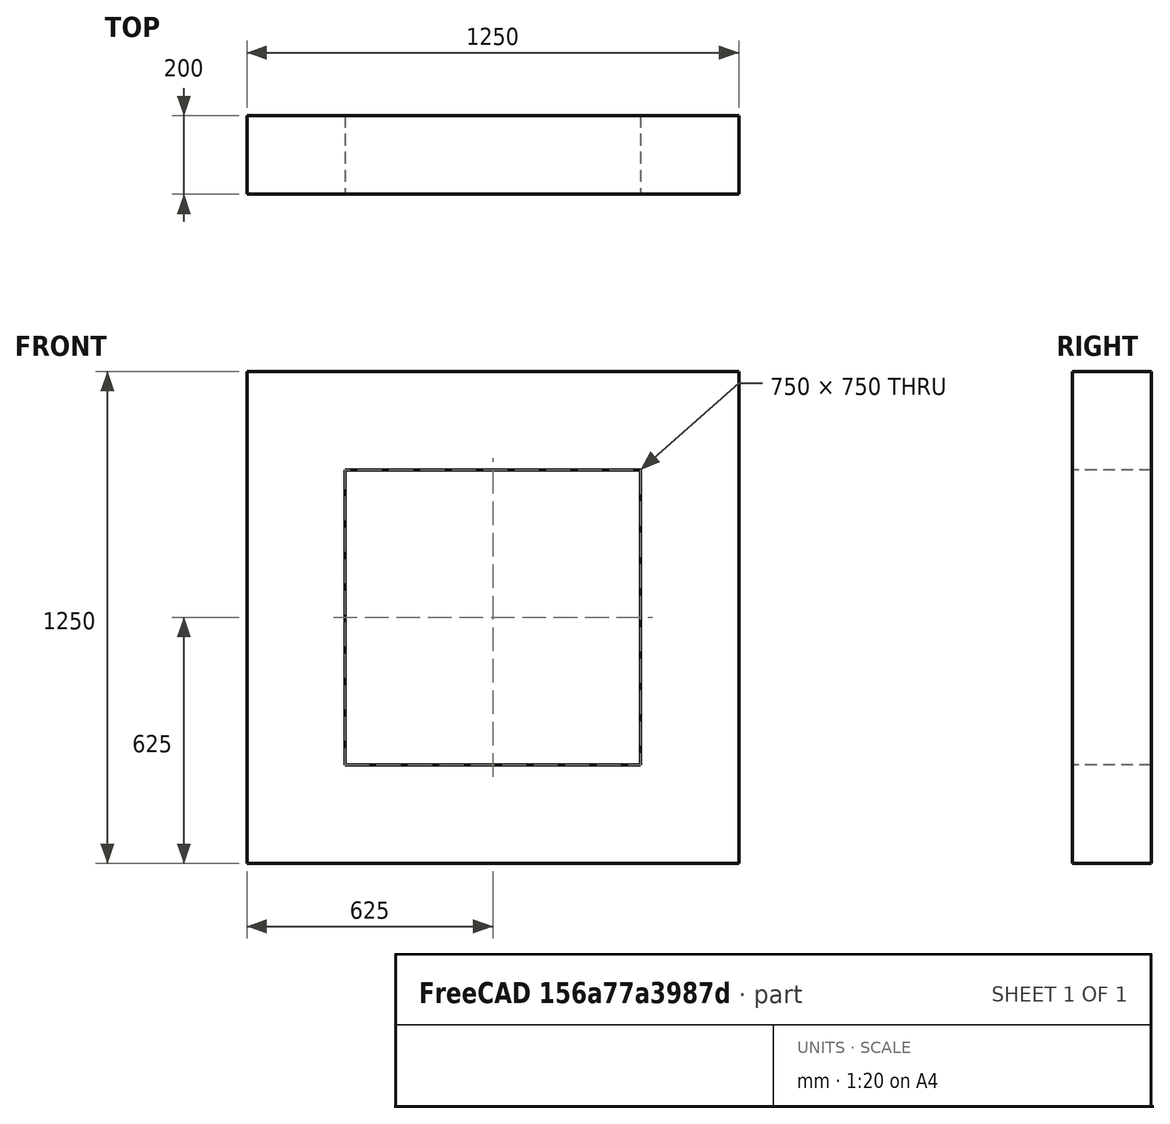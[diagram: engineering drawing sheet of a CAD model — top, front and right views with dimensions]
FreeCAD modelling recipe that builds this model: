
FCSTD DOCUMENT  (FreeCAD 0.20R29410 (Git))
Label: gates
License: All rights reserved
LicenseURL: http://en.wikipedia.org/wiki/All_rights_reserved
objects: Sketcher::SketchObject×1, PartDesign::Pad×1, PartDesign::Body×1
note: 4 computed .brp shape members not serialized (recipe doc carries the construction recipe); baked Part::Feature solids carry a one-line shape summary decoded from their .brp

FEATURE [Sketcher::SketchObject] Sketch
  FullyConstrained = true
  MapMode = 5
  Placement = pos=(0,0,0) rot=(1,0,0;1.5708rad)
  Support = -> [XZ_Plane001]
  sketch-geometry (8):
    g0: LineSegment StartX=-625 StartY=625 StartZ=0 EndX=625 EndY=625 EndZ=0
    g1: LineSegment StartX=625 StartY=625 StartZ=0 EndX=625 EndY=-625 EndZ=0
    g2: LineSegment StartX=625 StartY=-625 StartZ=0 EndX=-625 EndY=-625 EndZ=0
    g3: LineSegment StartX=-625 StartY=-625 StartZ=0 EndX=-625 EndY=625 EndZ=0
    g4: LineSegment StartX=-375 StartY=375 StartZ=0 EndX=375 EndY=375 EndZ=0
    g5: LineSegment StartX=375 StartY=375 StartZ=0 EndX=375 EndY=-375 EndZ=0
    g6: LineSegment StartX=375 StartY=-375 StartZ=0 EndX=-375 EndY=-375 EndZ=0
    g7: LineSegment StartX=-375 StartY=-375 StartZ=0 EndX=-375 EndY=375 EndZ=0
  constraints (24):
    c: Coincident(g0,g1)
    c: Coincident(g1,g2)
    c: Coincident(g2,g3)
    c: Coincident(g3,g0)
    c: Horizontal(g0)
    c: Horizontal(g2)
    c: Vertical(g1)
    c: Vertical(g3)
    c: Coincident(g4,g5)
    c: Coincident(g5,g6)
    c: Coincident(g6,g7)
    c: Coincident(g7,g4)
    c: Horizontal(g4)
    c: Horizontal(g6)
    c: Vertical(g5)
    c: Vertical(g7)
    c: Distance(g1,g0) = 1250
    c: Distance(g2,g1) = 1250
    c: Distance(g5,g4) = 750
    c: Distance(g5,g6) = 750
    c: Distance(g5,g1) = 250
    c: Distance(g6,g2) = 250
    c: Distance(g-1,g3) = 625
    c: Distance(g-1,g0) = 625
FEATURE [PartDesign::Pad] Pad
  Direction = (0,-1,2e-16)
  Length = 200
  Length2 = 10
  Placement = pos=(0,0,0) rot=(1,0,0;1.5708rad)
  Profile = -> Sketch
  ReferenceAxis = -> Sketch [N_Axis]
  Type = 0
FEATURE [PartDesign::Body] Body
  Group = -> [Sketch,Pad]
  Origin = -> Origin001
  Tip = -> Pad
